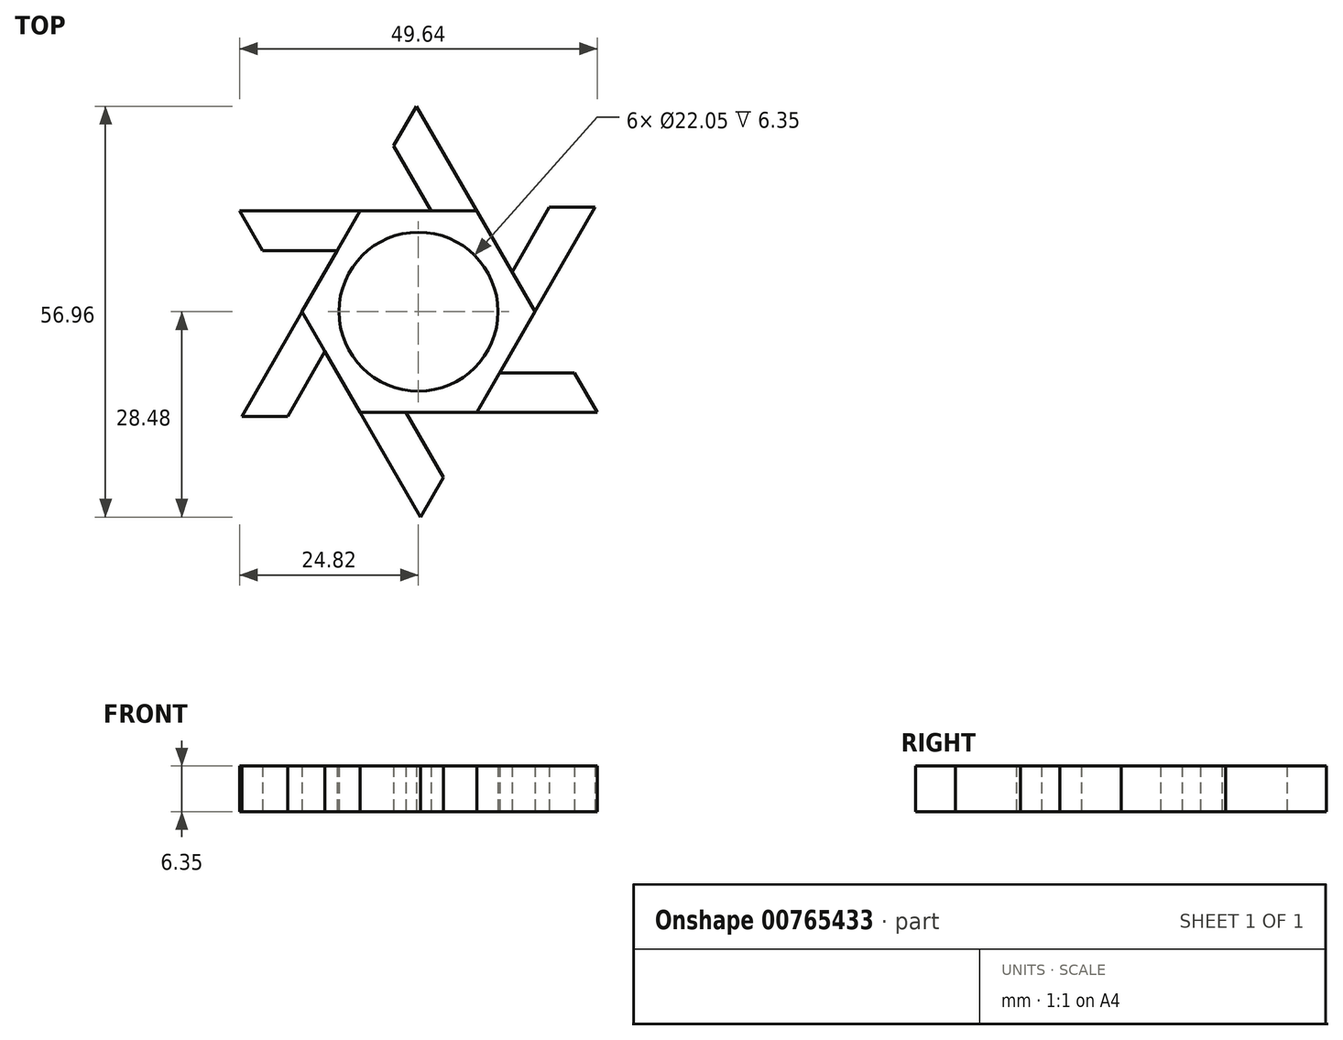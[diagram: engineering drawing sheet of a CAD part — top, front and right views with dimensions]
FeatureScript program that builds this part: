
annotation { "Feature Type Name" : "Feature", "Feature Type Description" : "" }
export const myFeature = defineFeature(function(context is Context, id is Id, definition is map)
    precondition{}
    {
        {
            var Q0;
            Q0=qCreatedBy(makeId("Top.planeOp"),FACE);
            var sketch = newSketch(context, id + "F0", { "sketchPlane" : qUnion([Q0])});
            skCircle(sketch, "E0.cCircle", {"center": v(0, 0) * mm, "radius": 13.97 * mm, "construction": true});
            skLineSegment(sketch, "E0.0", {"start": v(8.07, -13.97) * mm, "end": v(-8.07, -13.97) * mm});
            skLineSegment(sketch, "E0.1", {"start": v(-8.07, -13.97) * mm, "end": v(-16.13, 0) * mm});
            skLineSegment(sketch, "E0.2", {"start": v(-16.13, 0) * mm, "end": v(-8.07, 13.97) * mm});
            skLineSegment(sketch, "E0.3", {"start": v(-8.07, 13.97) * mm, "end": v(8.07, 13.97) * mm});
            skLineSegment(sketch, "E0.4", {"start": v(8.07, 13.97) * mm, "end": v(16.13, 0) * mm});
            skLineSegment(sketch, "E0.5", {"start": v(16.13, 0) * mm, "end": v(8.07, -13.97) * mm});
            skPoint(sketch, "E0.0.midPoint", {"position": v(0, -13.97) * mm});
            skCircle(sketch, "E1", {"center": v(0, 0) * mm, "radius": 11.02 * mm});
            skLineSegment(sketch, "E2", {"start": v(-16.13, 0) * mm, "end": v(6.73, -39.6) * mm});
            skLineSegment(sketch, "E3", {"start": v(-1.72, -13.97) * mm, "end": v(4.63, -24.97) * mm});
            skCircle(sketch, "E4.cCircle", {"center": v(13.14, -28.48) * mm, "radius": 11.11 * mm, "construction": true});
            skLineSegment(sketch, "E4.0", {"start": v(6.73, -39.6) * mm, "end": v(0.31, -28.48) * mm});
            skLineSegment(sketch, "E4.1", {"start": v(0.31, -28.48) * mm, "end": v(6.73, -17.37) * mm});
            skLineSegment(sketch, "E4.2", {"start": v(6.73, -17.37) * mm, "end": v(19.56, -17.37) * mm});
            skLineSegment(sketch, "E4.3", {"start": v(19.56, -17.37) * mm, "end": v(25.98, -28.48) * mm});
            skLineSegment(sketch, "E4.4", {"start": v(25.98, -28.48) * mm, "end": v(19.56, -39.6) * mm});
            skLineSegment(sketch, "E4.5", {"start": v(19.56, -39.6) * mm, "end": v(6.73, -39.6) * mm});
            skPoint(sketch, "E4.0.midPoint", {"position": v(3.52, -34.04) * mm});
            skCircle(sketch, "E5.cCircle", {"center": v(13.14, -28.48) * mm, "radius": 7.94 * mm, "construction": true});
            skLineSegment(sketch, "E5.0", {"start": v(17.73, -36.42) * mm, "end": v(8.56, -36.42) * mm});
            skLineSegment(sketch, "E5.1", {"start": v(8.56, -36.42) * mm, "end": v(3.98, -28.48) * mm});
            skLineSegment(sketch, "E5.2", {"start": v(3.98, -28.48) * mm, "end": v(8.56, -20.54) * mm});
            skLineSegment(sketch, "E5.3", {"start": v(8.56, -20.54) * mm, "end": v(17.73, -20.54) * mm});
            skLineSegment(sketch, "E5.4", {"start": v(17.73, -20.54) * mm, "end": v(22.31, -28.48) * mm});
            skLineSegment(sketch, "E5.5", {"start": v(22.31, -28.48) * mm, "end": v(17.73, -36.42) * mm});
            skPoint(sketch, "E5.0.midPoint", {"position": v(13.14, -36.42) * mm});
            skSolve(sketch);
        }
        {
            var Q0;
            {var subQ0=sQuery(id+"F0.wireOp",EDGE,"E0.2");Q0=makeQuery(id+"F0.imprint","IMPRINT",FACE,{"disambiguationData":[TD([[makeQuery(id+"F0.imprint","IMPRINT",EDGE,{"derivedFrom":subQ0}),-1.0]])]});}
            var Q1;
            {var subQ0=sQuery(id+"F0.wireOp",EDGE,"E2");var subQ1=sQuery(id+"F0.wireOp",EDGE,"E0.0");var subQ2=makeQuery(id+"F0.imprint","INTERSECT",VERTEX,{"derivedFrom":[subQ1,subQ0]});Q1=makeQuery(id+"F0.imprint","IMPRINT",FACE,{"disambiguationData":[TD([[makeQuery(id+"F0.imprint","IMPRINT",EDGE,{"disambiguationData":[TD([[subQ2,1.0]])],"derivedFrom":subQ1}),1.0]])]});}
            var Q2;
            {var subQ0=sQuery(id+"F0.wireOp",EDGE,"E4.0");Q2=makeQuery(id+"F0.imprint","IMPRINT",FACE,{"disambiguationData":[TD([[makeQuery(id+"F0.imprint","IMPRINT",EDGE,{"derivedFrom":subQ0}),-1.0]])]});}
            extrude(context, id + "F1", {"entities" : qUnion([Q0, Q1, Q2]), "depth" : 6.35 * mm, "offsetDistance" : 25.4 * mm});
        }
        {
            var Q0;
            Q0=makeQuery(id+"F1.opExtrude","SWEPT_BODY",BODY,{"disambiguationData":[OSD([sQuery(id+"F0.wireOp",EDGE,"E0.0"),sQuery(id+"F0.wireOp",EDGE,"E0.2"),sQuery(id+"F0.wireOp",EDGE,"E0.3"),sQuery(id+"F0.wireOp",EDGE,"E0.4"),sQuery(id+"F0.wireOp",EDGE,"E0.5"),sQuery(id+"F0.wireOp",EDGE,"E1"),sQuery(id+"F0.wireOp",EDGE,"E2"),sQuery(id+"F0.wireOp",EDGE,"E3"),sQuery(id+"F0.wireOp",EDGE,"E4.0"),sQuery(id+"F0.wireOp",EDGE,"E4.1"),sQuery(id+"F0.wireOp",EDGE,"E4.2"),sQuery(id+"F0.wireOp",EDGE,"E4.3"),sQuery(id+"F0.wireOp",EDGE,"E4.4"),sQuery(id+"F0.wireOp",EDGE,"E4.5"),sQuery(id+"F0.wireOp",EDGE,"E5.0"),sQuery(id+"F0.wireOp",EDGE,"E5.1"),sQuery(id+"F0.wireOp",EDGE,"E5.2"),sQuery(id+"F0.wireOp",EDGE,"E5.3"),sQuery(id+"F0.wireOp",EDGE,"E5.4"),sQuery(id+"F0.wireOp",EDGE,"E5.5")])]});
            var Q1;
            Q1=makeQuery(id+"F1.opExtrude","CAP_EDGE",EDGE,{"disambiguationData":[OSD([sQuery(id+"F0.wireOp",EDGE,"E1")])],"isStart":false});
            circularPattern(context, id + "F2", {"entities" : qUnion([Q0]), "axis" : qUnion([Q1]), "angle" : 360 * degree, "instanceCount" : 6, "equalSpace" : true});
        }
    });
